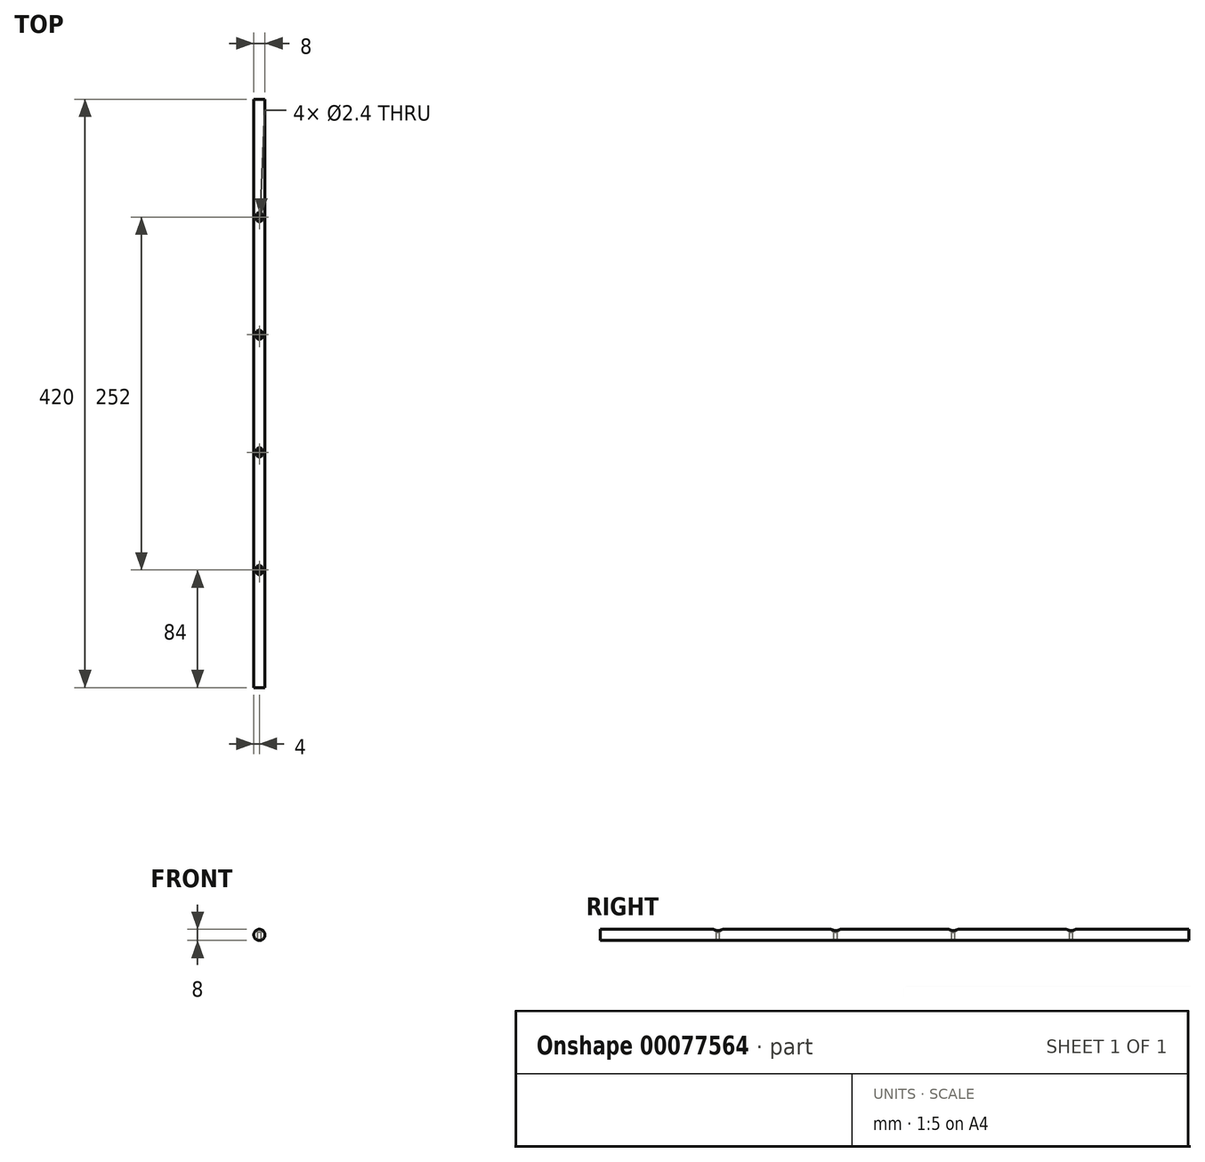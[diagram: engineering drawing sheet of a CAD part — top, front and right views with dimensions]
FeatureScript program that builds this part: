
annotation { "Feature Type Name" : "Feature", "Feature Type Description" : "" }
export const myFeature = defineFeature(function(context is Context, id is Id, definition is map)
    precondition{}
    {
        {
            var Q0;
            Q0=qCreatedBy(makeId("Front.planeOp"),FACE);
            var sketch = newSketch(context, id + "F0", { "sketchPlane" : qUnion([Q0])});
            skCircle(sketch, "E0", {"center": v(0, 0) * mm, "radius": 4 * mm});
            skSolve(sketch);
        }
        {
            var Q0;
            Q0=makeQuery(id+"F0.imprint","IMPRINT",FACE,{"disambiguationData":[TD([[makeQuery(id+"F0.imprint","IMPRINT",EDGE,{"derivedFrom":sQuery(id+"F0.wireOp",EDGE,"E0")}),1.0]])]});
            extrude(context, id + "F1", {"entities" : qUnion([Q0]), "oppositeDirection" : true, "depth" : 420 * mm});
        }
        {
            var Q0;
            Q0=qCreatedBy(makeId("Top.planeOp"),FACE);
            cPlane(context, id + "F2", {"entities" : qUnion([Q0]), "cplaneType" : CPlaneType.OFFSET, "offset" : 4 * mm, "width" : 150 * mm, "height" : 150 * mm});
        }
        {
            var Q0;
            Q0=qCreatedBy(id+"F2.planeOp",FACE);
            var sketch = newSketch(context, id + "F3", { "sketchPlane" : qUnion([Q0])});
            skPoint(sketch, "E1", {"position": v(0, 84) * mm});
            skPoint(sketch, "E2.0.1.0", {"position": v(0, 168) * mm});
            skPoint(sketch, "E2.0.2.0", {"position": v(0, 252) * mm});
            skPoint(sketch, "E2.0.3.0", {"position": v(0, 336) * mm});
            skLineSegment(sketch, "E2.direction1", {"start": v(0, 84) * mm, "end": v(25, 84) * mm, "construction": true});
            skLineSegment(sketch, "E2.direction2", {"start": v(0, 84) * mm, "end": v(0, 168) * mm, "construction": true});
            skSolve(sketch);
        }
        {
            var Q0;
            Q0=sQuery(id+"F3.wireOp",VERTEX,"E1");
            var Q1;
            Q1=sQuery(id+"F3.wireOp",VERTEX,"E2.0.1.0");
            var Q2;
            Q2=sQuery(id+"F3.wireOp",VERTEX,"E2.0.2.0");
            var Q3;
            Q3=sQuery(id+"F3.wireOp",VERTEX,"E2.0.3.0");
            var Q4;
            Q4=makeQuery(id+"F1.opExtrude","SWEPT_BODY",BODY,{"disambiguationData":[OSD([sQuery(id+"F0.wireOp",EDGE,"E0")])]});
            hole(context, id + "F4", {"style" : HoleStyle.C_SINK, "endStyle" : HoleEndStyle.BLIND, "standardTappedOrClearance" : lookupTablePath({ "standard" : "ISO", "engagement" : "75%", "pitch" : "0.6 mm", "size" : "M3", "type" : "Tapped" }), "standardBlindInLast" : lookupTablePath({ "standard" : "ISO", "engagement" : "75%", "pitch" : "0.6 mm", "size" : "M3", "type" : "Tapped" }), "holeDiameter" : 2.4 * mm, "cSinkDiameter" : 6.72 * mm, "cSinkAngle" : 90 * degree, "holeDepth" : 100 * mm, "startFromSketch" : true, "locations" : qUnion([Q0, Q1, Q2, Q3]), "scope" : qUnion([Q4])});
        }
    });
